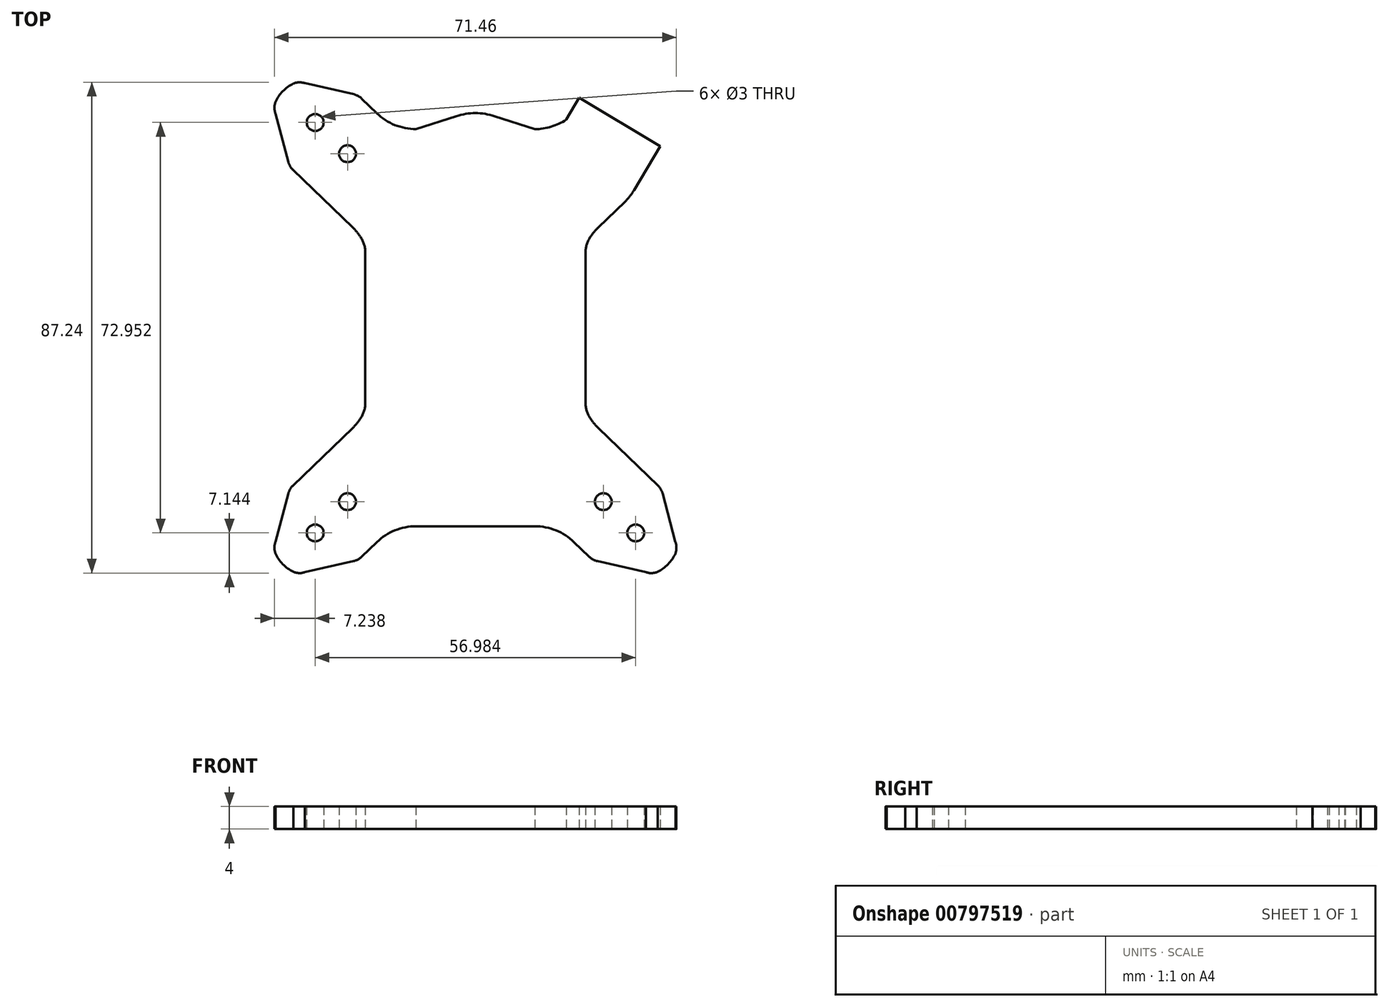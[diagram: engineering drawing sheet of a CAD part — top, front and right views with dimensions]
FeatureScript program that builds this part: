
annotation { "Feature Type Name" : "Feature", "Feature Type Description" : "" }
export const myFeature = defineFeature(function(context is Context, id is Id, definition is map)
    precondition{}
    {
        {
            var Q0;
            Q0=qCreatedBy(makeId("Top.planeOp"),FACE);
            var sketch = newSketch(context, id + "F0", { "sketchPlane" : qUnion([Q0])});
            skPoint(sketch, "E0.MirrorP", {"position": v(-36.6, 44.19) * mm});
            skArc(sketch, "E1.MirrorCS", {"start": v(21.65, -41.5) * mm, "mid": v(20.88, -41.2) * mm, "end": v(20.23, -40.73) * mm});
            skArc(sketch, "E2.MirrorCS", {"start": v(32.4, -43.4) * mm, "mid": v(31.36, -43.62) * mm, "end": v(30.33, -43.46) * mm});
            skLineSegment(sketch, "E3.MirrorCS", {"start": v(19.47, -40) * mm, "end": v(20.23, -40.73) * mm});
            skArc(sketch, "E4.MirrorCS", {"start": v(35.55, -40.13) * mm, "mid": v(34.25, -42.03) * mm, "end": v(32.4, -43.4) * mm});
            skLineSegment(sketch, "E5.MirrorCS", {"start": v(30.33, -43.46) * mm, "end": v(25.04, -42.26) * mm});
            skLineSegment(sketch, "E6.MirrorCS", {"start": v(25.04, -42.26) * mm, "end": v(21.65, -41.5) * mm});
            skLineSegment(sketch, "E7.MirrorCS", {"start": v(34.15, -32.83) * mm, "end": v(33.26, -29.46) * mm});
            skArc(sketch, "E8.MirrorCS", {"start": v(32.45, -28.06) * mm, "mid": v(32.95, -28.7) * mm, "end": v(33.26, -29.46) * mm});
            skArc(sketch, "E9.MirrorCS", {"start": v(35.55, -40.13) * mm, "mid": v(35.73, -39.1) * mm, "end": v(35.54, -38.06) * mm});
            skPoint(sketch, "E10.MirrorP", {"position": v(22.43, -40.22) * mm});
            skPoint(sketch, "E11.MirrorP", {"position": v(32.4, -43.4) * mm});
            skPoint(sketch, "E12.MirrorP", {"position": v(30.54, -43.92) * mm});
            skPoint(sketch, "E13.MirrorP", {"position": v(24.73, -42.98) * mm});
            skLineSegment(sketch, "E14.MirrorCS", {"start": v(35.54, -38.06) * mm, "end": v(34.15, -32.83) * mm});
            skPoint(sketch, "E15.MirrorP", {"position": v(22.28, -40.68) * mm});
            skPoint(sketch, "E16.MirrorP", {"position": v(25.51, -43.08) * mm});
            skPoint(sketch, "E17.MirrorP", {"position": v(23.72, -41.46) * mm});
            skPoint(sketch, "E18.MirrorP", {"position": v(34.15, -32.83) * mm});
            skPoint(sketch, "E19.MirrorP", {"position": v(20.84, -37.7) * mm});
            skPoint(sketch, "E20.MirrorP", {"position": v(20.83, -41.3) * mm});
            skPoint(sketch, "E21.MirrorP", {"position": v(34.4, -42.17) * mm});
            skPoint(sketch, "E22.MirrorP", {"position": v(32.61, -43.7) * mm});
            skPoint(sketch, "E23.MirrorP", {"position": v(33.3, -31.53) * mm});
            skPoint(sketch, "E24.MirrorP", {"position": v(35.82, -40.17) * mm});
            skPoint(sketch, "E25.MirrorP", {"position": v(25.04, -42.26) * mm});
            skPoint(sketch, "E26.MirrorP", {"position": v(35.83, -38.8) * mm});
            skPoint(sketch, "E27.MirrorP", {"position": v(24.1, -42.43) * mm});
            skPoint(sketch, "E28.MirrorP", {"position": v(33.05, -28.65) * mm});
            skCircle(sketch, "E29.MirrorC", {"center": v(28.5, -36.48) * mm, "radius": 1.5 * mm});
            skLineSegment(sketch, "E30.MirrorCS", {"start": v(19.47, -40) * mm, "end": v(17.5, -38.1) * mm});
            skPoint(sketch, "E31.MirrorCS.end.orphan", {"position": v(34.28, -42.07) * mm});
            skPoint(sketch, "E31.MirrorCS.start.orphan", {"position": v(34.35, -42) * mm});
            skLineSegment(sketch, "E32.MirrorCS", {"start": v(-19.47, -40) * mm, "end": v(-20.23, -40.73) * mm});
            skArc(sketch, "E33.MirrorCS", {"start": v(-21.65, -41.5) * mm, "mid": v(-20.88, -41.2) * mm, "end": v(-20.23, -40.73) * mm});
            skArc(sketch, "E34.MirrorCS", {"start": v(-32.45, -28.06) * mm, "mid": v(-32.95, -28.7) * mm, "end": v(-33.26, -29.46) * mm});
            skArc(sketch, "E35.MirrorCS", {"start": v(-32.4, -43.4) * mm, "mid": v(-31.36, -43.62) * mm, "end": v(-30.33, -43.46) * mm});
            skLineSegment(sketch, "E36.MirrorCS", {"start": v(-25.04, -42.26) * mm, "end": v(-21.65, -41.5) * mm});
            skArc(sketch, "E37.MirrorCS", {"start": v(-35.55, -40.13) * mm, "mid": v(-35.73, -39.1) * mm, "end": v(-35.54, -38.06) * mm});
            skLineSegment(sketch, "E38.MirrorCS", {"start": v(-34.15, -32.83) * mm, "end": v(-33.26, -29.46) * mm});
            skPoint(sketch, "E39.MirrorP", {"position": v(-32.4, -43.4) * mm});
            skPoint(sketch, "E40.MirrorP", {"position": v(-33.3, -31.53) * mm});
            skArc(sketch, "E41.MirrorCS", {"start": v(-35.55, -40.13) * mm, "mid": v(-34.25, -42.03) * mm, "end": v(-32.4, -43.4) * mm});
            skPoint(sketch, "E42.MirrorP", {"position": v(-34.4, -42.17) * mm});
            skPoint(sketch, "E43.MirrorP", {"position": v(-34.15, -32.83) * mm});
            skCircle(sketch, "E44.MirrorC", {"center": v(-28.5, -36.48) * mm, "radius": 1.5 * mm});
            skLineSegment(sketch, "E45.MirrorCS", {"start": v(-35.54, -38.06) * mm, "end": v(-34.15, -32.83) * mm});
            skPoint(sketch, "E46.MirrorP", {"position": v(-23.72, -41.46) * mm});
            skLineSegment(sketch, "E47.MirrorCS", {"start": v(-30.33, -43.46) * mm, "end": v(-25.04, -42.26) * mm});
            skPoint(sketch, "E48.MirrorP", {"position": v(-33.05, -28.65) * mm});
            skPoint(sketch, "E49.MirrorP", {"position": v(-30.54, -43.92) * mm});
            skPoint(sketch, "E50.MirrorP", {"position": v(-32.83, -27.83) * mm});
            skLineSegment(sketch, "E51.MirrorCS", {"start": v(-19.47, -40) * mm, "end": v(-17.5, -38.1) * mm});
            skPoint(sketch, "E52.MirrorP", {"position": v(-20.83, -41.3) * mm});
            skPoint(sketch, "E53.MirrorP", {"position": v(-34.28, -42.07) * mm});
            skPoint(sketch, "E54.MirrorP", {"position": v(-27.16, -26.37) * mm});
            skLineSegment(sketch, "E55.MirrorCS", {"start": v(-19.47, 40) * mm, "end": v(-20.23, 40.73) * mm});
            skArc(sketch, "E56.MirrorCS", {"start": v(-21.65, 41.5) * mm, "mid": v(-20.88, 41.2) * mm, "end": v(-20.23, 40.73) * mm});
            skArc(sketch, "E57.MirrorCS", {"start": v(-32.4, 43.4) * mm, "mid": v(-31.36, 43.62) * mm, "end": v(-30.33, 43.46) * mm});
            skLineSegment(sketch, "E58.MirrorCS", {"start": v(-25.04, 42.26) * mm, "end": v(-21.65, 41.5) * mm});
            skLineSegment(sketch, "E59.MirrorCS", {"start": v(-34.15, 32.83) * mm, "end": v(-33.26, 29.46) * mm});
            skArc(sketch, "E60.MirrorCS", {"start": v(-35.55, 40.13) * mm, "mid": v(-35.73, 39.1) * mm, "end": v(-35.54, 38.06) * mm});
            skArc(sketch, "E61.MirrorCS", {"start": v(-32.45, 28.06) * mm, "mid": v(-32.95, 28.7) * mm, "end": v(-33.26, 29.46) * mm});
            skArc(sketch, "E62.MirrorCS", {"start": v(-35.55, 40.13) * mm, "mid": v(-34.25, 42.03) * mm, "end": v(-32.4, 43.4) * mm});
            skCircle(sketch, "E63.MirrorC", {"center": v(-28.5, 36.48) * mm, "radius": 1.5 * mm});
            skCircle(sketch, "E64.MirrorC", {"center": v(-22.74, 30.92) * mm, "radius": 1.5 * mm});
            skLineSegment(sketch, "E65.MirrorCS", {"start": v(-30.33, 43.46) * mm, "end": v(-25.04, 42.26) * mm});
            skPoint(sketch, "E66.MirrorP", {"position": v(-27.16, 26.37) * mm});
            skPoint(sketch, "E67.MirrorP", {"position": v(-25.04, 42.26) * mm});
            skLineSegment(sketch, "E68.MirrorCS", {"start": v(-19.47, 40) * mm, "end": v(-17.5, 38.1) * mm});
            skLineSegment(sketch, "E69.MirrorCS", {"start": v(-35.54, 38.06) * mm, "end": v(-34.15, 32.83) * mm});
            skPoint(sketch, "E70.MirrorP", {"position": v(-33.3, 31.53) * mm});
            skPoint(sketch, "E71.MirrorP", {"position": v(-20.83, 41.3) * mm});
            skPoint(sketch, "E72.MirrorP", {"position": v(-32.4, 43.4) * mm});
            skPoint(sketch, "E73.MirrorP", {"position": v(-15.05, 21.64) * mm});
            skPoint(sketch, "E74.MirrorP", {"position": v(-34.15, 32.83) * mm});
            skPoint(sketch, "E75.middle", {"position": v(0, 0) * mm});
            skPoint(sketch, "E76.MirrorCS.end.orphan", {"position": v(25.22, -21.09) * mm});
            skLineSegment(sketch, "E77", {"start": v(32.45, -28.06) * mm, "end": v(21.83, -17.82) * mm});
            skLineSegment(sketch, "E78.MirrorCS", {"start": v(-32.45, -28.06) * mm, "end": v(-21.83, -17.82) * mm});
            skLineSegment(sketch, "E79.MirrorCS", {"start": v(-32.45, 28.06) * mm, "end": v(-21.83, 17.82) * mm});
            skPoint(sketch, "E80.visualSharp", {"position": v(18.78, -14.87) * mm});
            skArc(sketch, "E80.filletArc", {"start": v(20.37, -16.04) * mm, "mid": v(21.05, -16.97) * mm, "end": v(21.83, -17.82) * mm});
            skArc(sketch, "E81.filletArc", {"start": v(21.83, 17.82) * mm, "mid": v(21.05, 16.97) * mm, "end": v(20.37, 16.04) * mm});
            skPoint(sketch, "E82.visualSharp", {"position": v(-18.78, -14.87) * mm});
            skArc(sketch, "E82.filletArc", {"start": v(-21.83, -17.82) * mm, "mid": v(-21.05, -16.97) * mm, "end": v(-20.37, -16.04) * mm});
            skPoint(sketch, "E83.visualSharp", {"position": v(-18.78, 14.87) * mm});
            skArc(sketch, "E83.filletArc", {"start": v(-20.37, 16.04) * mm, "mid": v(-21.05, 16.97) * mm, "end": v(-21.83, 17.82) * mm});
            skLineSegment(sketch, "E84", {"start": v(10.56, -35.3) * mm, "end": v(-10.56, -35.3) * mm});
            skPoint(sketch, "E85.visualSharp", {"position": v(14.6, -35.3) * mm});
            skArc(sketch, "E85.filletArc", {"start": v(17.5, -38.1) * mm, "mid": v(14.3, -36.03) * mm, "end": v(10.56, -35.3) * mm});
            skPoint(sketch, "E86.visualSharp", {"position": v(-14.6, -35.3) * mm});
            skArc(sketch, "E86.filletArc", {"start": v(-10.56, -35.3) * mm, "mid": v(-14.3, -36.03) * mm, "end": v(-17.5, -38.1) * mm});
            skPoint(sketch, "E87", {"position": v(0, 9.33) * mm});
            skPoint(sketch, "E88.MirrorP", {"position": v(-14.6, 35.3) * mm});
            skPoint(sketch, "E89.MirrorP", {"position": v(14.6, 35.3) * mm});
            skArc(sketch, "E90.MirrorCS", {"start": v(-10.56, 35.3) * mm, "mid": v(-14.3, 36.03) * mm, "end": v(-17.5, 38.1) * mm});
            skArc(sketch, "E91.MirrorCS", {"start": v(16.12, 36.98) * mm, "mid": v(13.47, 35.73) * mm, "end": v(10.56, 35.3) * mm});
            skPoint(sketch, "E92.MirrorP", {"position": v(18.78, 14.87) * mm});
            skLineSegment(sketch, "E93.MirrorCS", {"start": v(26.55, 22.38) * mm, "end": v(21.83, 17.82) * mm});
            skCircle(sketch, "E94.MirrorC", {"center": v(-22.74, -30.92) * mm, "radius": 1.5 * mm});
            skCircle(sketch, "E95.MirrorC", {"center": v(22.74, -30.92) * mm, "radius": 1.5 * mm});
            skLineSegment(sketch, "E96", {"start": v(-19.57, 13.33) * mm, "end": v(-19.57, -13.33) * mm});
            skLineSegment(sketch, "E97.MirrorCS", {"start": v(19.57, 13.33) * mm, "end": v(19.57, -13.33) * mm});
            skPoint(sketch, "E98.visualSharp", {"position": v(19.57, 14.53) * mm});
            skArc(sketch, "E98.filletArc", {"start": v(20.37, 16.04) * mm, "mid": v(19.77, 14.74) * mm, "end": v(19.57, 13.33) * mm});
            skPoint(sketch, "E99.visualSharp", {"position": v(-19.57, 14.53) * mm});
            skArc(sketch, "E99.filletArc", {"start": v(-19.57, 13.33) * mm, "mid": v(-19.77, 14.74) * mm, "end": v(-20.37, 16.04) * mm});
            skPoint(sketch, "E100.orphan", {"position": v(19.57, -14.87) * mm});
            skPoint(sketch, "E101.visualSharp", {"position": v(19.57, -14.53) * mm});
            skArc(sketch, "E101.filletArc", {"start": v(19.57, -13.33) * mm, "mid": v(19.77, -14.74) * mm, "end": v(20.37, -16.04) * mm});
            skPoint(sketch, "E102.orphan", {"position": v(-19.57, -14.87) * mm});
            skPoint(sketch, "E103.visualSharp", {"position": v(-19.57, -14.53) * mm});
            skArc(sketch, "E103.filletArc", {"start": v(-20.37, -16.04) * mm, "mid": v(-19.77, -14.74) * mm, "end": v(-19.57, -13.33) * mm});
            skLineSegment(sketch, "E104", {"start": v(16.12, 36.98) * mm, "end": v(18.45, 40.9) * mm});
            skLineSegment(sketch, "E105", {"start": v(28.2, 24.44) * mm, "end": v(32.87, 32.28) * mm});
            skPoint(sketch, "E106.visualSharp", {"position": v(27.51, 23.3) * mm});
            skArc(sketch, "E106.filletArc", {"start": v(26.55, 22.38) * mm, "mid": v(27.44, 23.35) * mm, "end": v(28.2, 24.44) * mm});
            skLineSegment(sketch, "E107", {"start": v(-10.56, 35.3) * mm, "end": v(-3.4, 37.6) * mm});
            skLineSegment(sketch, "E108", {"start": v(3.4, 37.6) * mm, "end": v(10.56, 35.3) * mm});
            skPoint(sketch, "E109.visualSharp", {"position": v(0, 38.7) * mm});
            skArc(sketch, "E109.filletArc", {"start": v(3.4, 37.6) * mm, "mid": v(0, 38.14) * mm, "end": v(-3.4, 37.6) * mm});
            skLineSegment(sketch, "E110", {"start": v(25.66, 36.58) * mm, "end": v(18.25, 24.17) * mm, "construction": true});
            skLineSegment(sketch, "E111", {"start": v(18.45, 40.9) * mm, "end": v(32.87, 32.28) * mm});
            skSolve(sketch);
        }
        {
            var Q0;
            Q0 = qSketchRegion(id + "F0", true);
            extrude(context, id + "F1", {"entities" : qUnion([Q0]), "depth" : 4 * mm, "offsetDistance" : 25 * mm});
        }
    });
